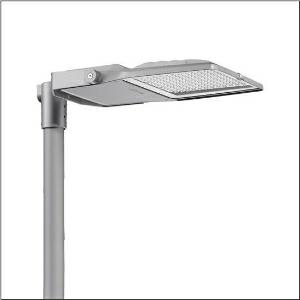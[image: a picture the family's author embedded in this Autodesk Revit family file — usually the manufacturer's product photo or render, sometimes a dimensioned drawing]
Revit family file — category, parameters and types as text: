
# Revit family: floodlight_fl_21_iq_midi___pl43_5xa7782f2a3a_db1b
name_source: partatom
category: Lighting Fixtures
units: mm (PartAtom-declared; Revit-internal decimal feet)

## family parameters
Cut with Voids When Loaded = No
Host = Face
Light Source = No
Part Type = Normal
Room Calculation Point = No
Round Connector Dimension = Use Diameter
Shared = No

## types (1)
- --- (1 x LED, 36680 lm, 270.2 W, 3000K)
    Apparent Load = 270 VA
    CIE Flux Codes = 27 78 99 100 100
    Color Rendering = 70
    Color Temperature = 3000K
    Default Elevation = 1800 mm
    Description = Floodlight FL 21 iQ midi, floodlight, primary light control with lens, of PMMA, primary optical cover: protective disc, of toughened safety glass, transparent, light distribution: PL43, light emission: direct distribution, installation type: surface-mounted, LED, High Power LED, rated luminous flux: 36.680lm, luminous efficacy: 136lm/W, light colour: 730, colour temperature: 3000K, control gear: iQ Street-Remote/DALI, control: optimised constant luminous flux control (CLO 2.0), Desk-Remote (wireless, voltage-free reading and setting of iQ features in the workshop via application-optimized NFC function/RFID function), Smart-Wire, Night-Set, Temp-Guard, Auto-Match, Street-Remote, with terminal, 6-pole, mains connection: 220..240V, AC, 50/60Hz, start of lifetime: 270W, end of service life: 287W, reduction: 117W, luminaire housing, of diecast aluminium, powder-coated, Siteco® metallic grey (DB 702S), corrosivity category C5 mid according to DIN EN ISO 12944, suitable for swimming pools, chlorine-resistant, sealing non-destructively replaceable, please order mast flange separately, mast bracket, of steel, galvanised, powder-coated, Siteco® metallic grey (DB 702S), protection rating (complete): IP66, insulation class (complete): insulation class II (safety insulation), certification: CE, ENEC, VDE, protection symbol: D, impact resistance: IK08, permissible operating ambient temperature: -40..+40°C, permissible operating ambient temperature for outdoor applications: -40..+50°C, standard: DIN EN 12944, LABS conformity tested according to VDMA 24364:2018-05, packaging unit: 1 piece

Light Distribution: PL43
    Height = 76 mm
    Lamp = 1 x LED
    Lamp Light Flux = 36680 lm
    Lamp Power = 270.2 W
    Lamp count = 1
    Length = 657 mm
    Luminous efficacy = 136 lm/W
    Manufacturer = Siteco
    ModVariant = No
    Model = 5XA7782F2A3A
    Number of Poles = 1
    OnlyDefault = Yes
    Power Factor = 1
    Product Name = Floodlight FL 21 iQ midi | PL43
    Product group = floodlight | pylon annexe
    ProductGroupID = 6200
    Protection Class = Protection class II
    Protection Degree = IP 66
    RLX_Detail_Level = 1
    RLX_Emergency_Light_Flux = 0 lm
    RLX_Emergency_Type = 0
    RLX_Emergency_Type_DB = No
    RlxData = <blob elided: 153813 chars, md5=bb7c3b6f>
    Socket = socket
    Standby Power = 0 W
    System Light Flux = 36680 lm
    System Power = 270 W
    Type Comments = factory setting: luminous flux: 100 % | dim-lin: 254 | 620 mA
    Type Image = l_1007123.jpg
    URL = http://relux.com
    VarID = @adj_104698
    Voltage = 0 V
    Weight = 0.00 kg
    Width = 442 mm

## geometry (parser evidence)
native form markers: Blend x4, Sweep x12
no freeform markers — native parametric forms only
